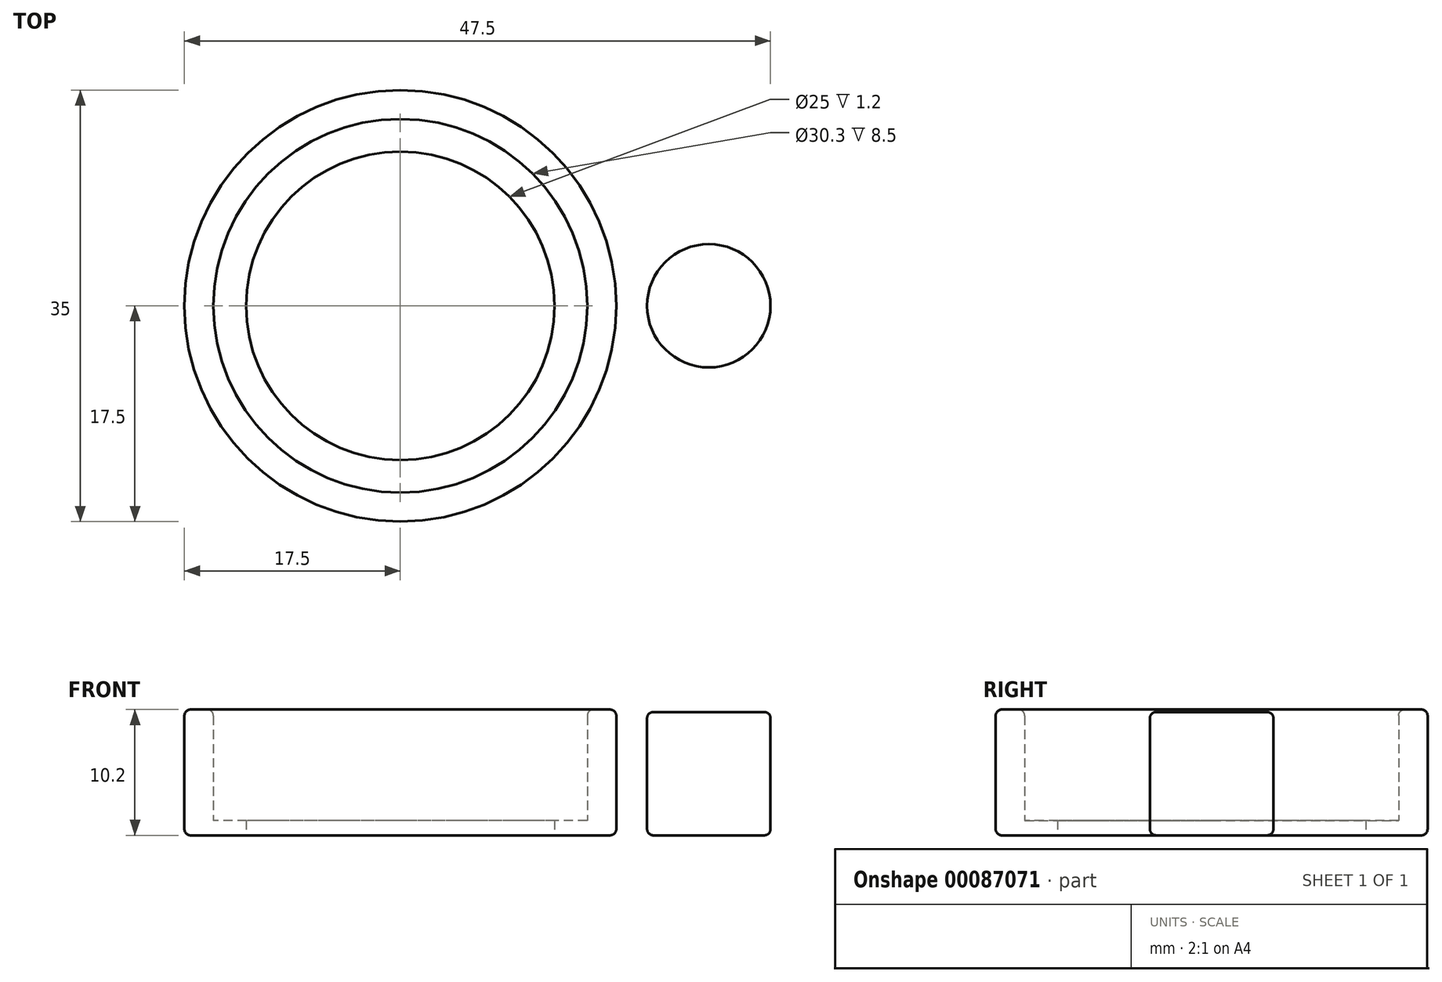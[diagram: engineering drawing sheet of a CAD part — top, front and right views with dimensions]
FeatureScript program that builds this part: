
annotation { "Feature Type Name" : "Feature", "Feature Type Description" : "" }
export const myFeature = defineFeature(function(context is Context, id is Id, definition is map)
    precondition{}
    {
        {
            var Q0;
            Q0=qCreatedBy(makeId("Top.planeOp"),FACE);
            var sketch = newSketch(context, id + "F0", { "sketchPlane" : qUnion([Q0])});
            skCircle(sketch, "E0", {"center": v(0, 0) * mm, "radius": 17.5 * mm});
            skCircle(sketch, "E1", {"center": v(0, 0) * mm, "radius": 12.5 * mm});
            skSolve(sketch);
        }
        {
            var Q0;
            Q0 = qSketchRegion(id + "F0", true);
            extrude(context, id + "F1", {"entities" : qUnion([Q0]), "depth" : 1.2 * mm});
        }
        {
            var Q0;
            Q0=makeQuery(id+"F1.opExtrude","CAP_FACE",FACE,{"disambiguationData":[OSD([sQuery(id+"F0.wireOp",EDGE,"E0"),sQuery(id+"F0.wireOp",EDGE,"E1")])],"isStart":false});
            var sketch = newSketch(context, id + "F2", { "sketchPlane" : qUnion([Q0])});
            skCircle(sketch, "E2.0", {"center": v(0, 0) * mm, "radius": 17.5 * mm});
            skCircle(sketch, "E3", {"center": v(0, 0) * mm, "radius": 15.15 * mm});
            skSolve(sketch);
        }
        {
            var Q0;
            Q0=makeQuery(id+"F2.imprint","IMPRINT",FACE,{"disambiguationData":[TD([[makeQuery(id+"F2.imprint","IMPRINT",EDGE,{"derivedFrom":sQuery(id+"F2.wireOp",EDGE,"E2.0")}),1.0]])]});
            extrude(context, id + "F3", {"entities" : qUnion([Q0]), "operationType" : NewBodyOperationType.ADD, "depth" : 9 * mm});
        }
        {
            var Q0;
            Q0=makeQuery(id+"F3.opExtrude","CAP_EDGE",EDGE,{"disambiguationData":[OSD([sQuery(id+"F2.wireOp",EDGE,"E3")])],"isStart":false});
            var Q1;
            Q1=makeQuery(id+"F3.opExtrude","CAP_EDGE",EDGE,{"disambiguationData":[OSD([sQuery(id+"F2.wireOp",EDGE,"E2.0")])],"isStart":false});
            var Q2;
            Q2=makeQuery(id+"F1.opExtrude","CAP_EDGE",EDGE,{"disambiguationData":[OSD([sQuery(id+"F0.wireOp",EDGE,"E0")])],"isStart":true});
            fillet(context, id + "F4", {"entities" : qUnion([Q0, Q1, Q2]), "radius" : .5 * mm, "tangentPropagation" : true, "allowEdgeOverflow" : false});
        }
        {
            var Q0;
            Q0=qCreatedBy(makeId("Top.planeOp"),FACE);
            var sketch = newSketch(context, id + "F5", { "sketchPlane" : qUnion([Q0])});
            skCircle(sketch, "E4", {"center": v(25, 0) * mm, "radius": 5 * mm});
            skSolve(sketch);
        }
        {
            var Q0;
            Q0 = qSketchRegion(id + "F5", true);
            extrude(context, id + "F6", {"entities" : qUnion([Q0]), "depth" : 10 * mm});
        }
        {
            var Q0;
            Q0=makeQuery(id+"F6.opExtrude","SWEPT_FACE",FACE,{"disambiguationData":[OSD([sQuery(id+"F5.wireOp",EDGE,"E4")])]});
            fillet(context, id + "F7", {"entities" : qUnion([Q0]), "radius" : .5 * mm, "tangentPropagation" : true, "allowEdgeOverflow" : false});
        }
    });
